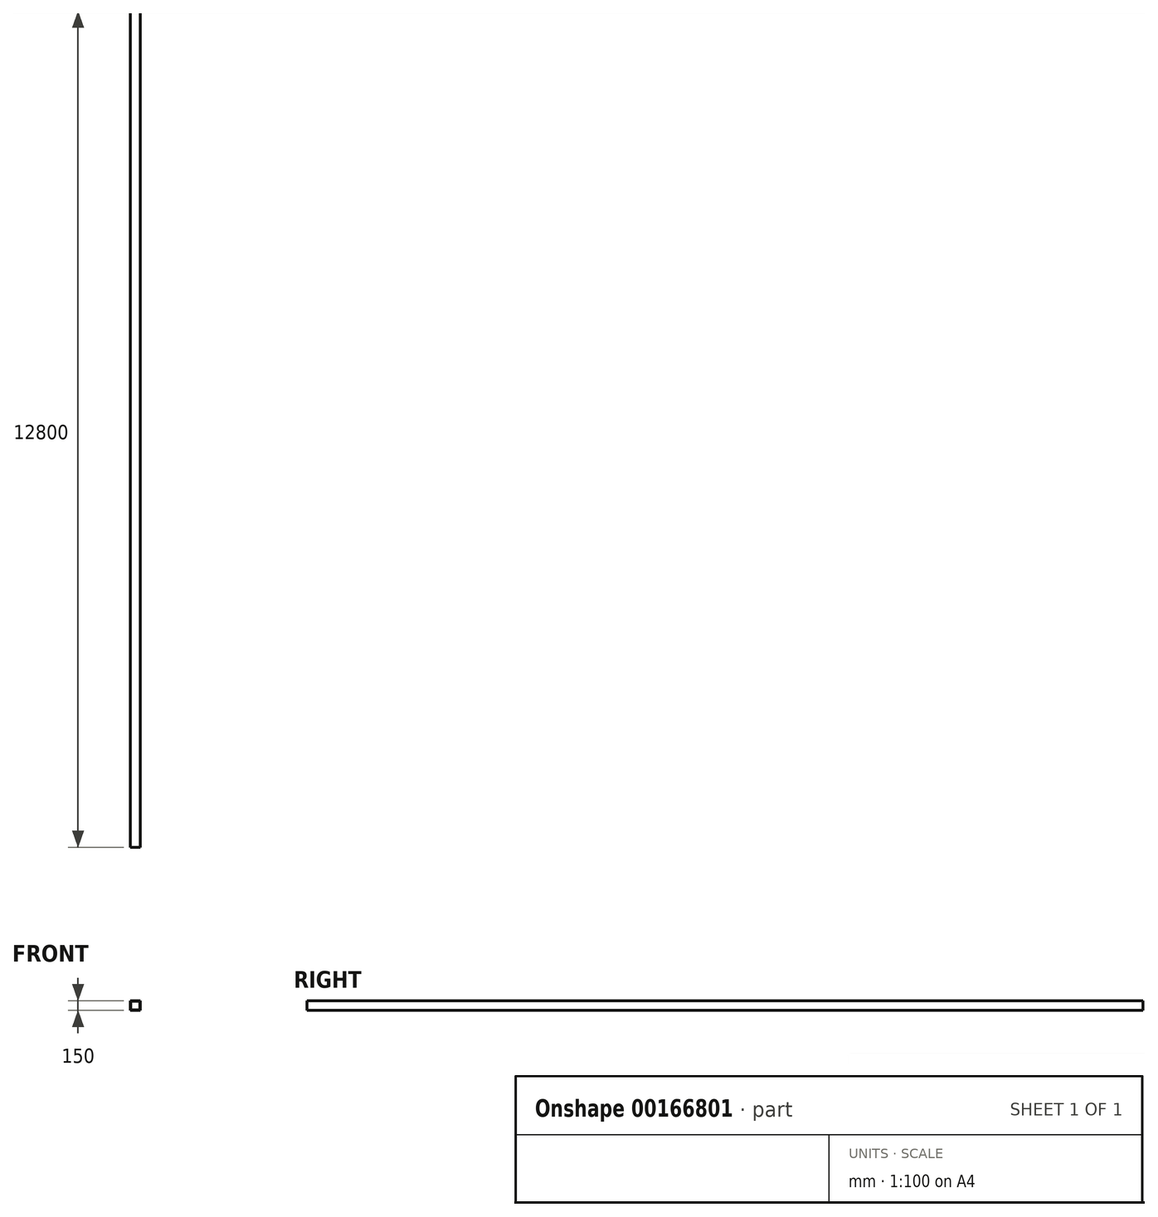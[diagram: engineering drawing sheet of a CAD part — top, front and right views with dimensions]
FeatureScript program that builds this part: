
annotation { "Feature Type Name" : "Feature", "Feature Type Description" : "" }
export const myFeature = defineFeature(function(context is Context, id is Id, definition is map)
    precondition{}
    {
        {
            var Q0;
            Q0=qCreatedBy(makeId("Front.planeOp"),FACE);
            var sketch = newSketch(context, id + "F0", { "sketchPlane" : qUnion([Q0])});
            skLineSegment(sketch, "E0.bottom", {"start": v(0, 0) * mm, "end": v(150, 0) * mm});
            skLineSegment(sketch, "E0.top", {"start": v(0, 150) * mm, "end": v(150, 150) * mm});
            skLineSegment(sketch, "E0.left", {"start": v(0, 0) * mm, "end": v(0, 150) * mm});
            skLineSegment(sketch, "E0.right", {"start": v(150, 0) * mm, "end": v(150, 150) * mm});
            skLineSegment(sketch, "E1.0", {"start": v(6, 6) * mm, "end": v(6, 144) * mm});
            skLineSegment(sketch, "E1.1", {"start": v(6, 6) * mm, "end": v(144, 6) * mm});
            skLineSegment(sketch, "E1.2", {"start": v(144, 6) * mm, "end": v(144, 144) * mm});
            skLineSegment(sketch, "E1.3", {"start": v(6, 144) * mm, "end": v(144, 144) * mm});
            skSolve(sketch);
        }
        {
            var Q0;
            Q0 = qSketchRegion(id + "F0", true);
            var Q1;
            Q1=makeQuery(id+"F0.imprint","IMPRINT",FACE,{"disambiguationData":[TD([[makeQuery(id+"F0.imprint","IMPRINT",EDGE,{"derivedFrom":sQuery(id+"F0.wireOp",EDGE,"E0.bottom")}),1.0]])]});
            extrude(context, id + "F1", {"entities" : qUnion([Q0, Q1]), "depth" : 12800 * mm});
        }
    });
